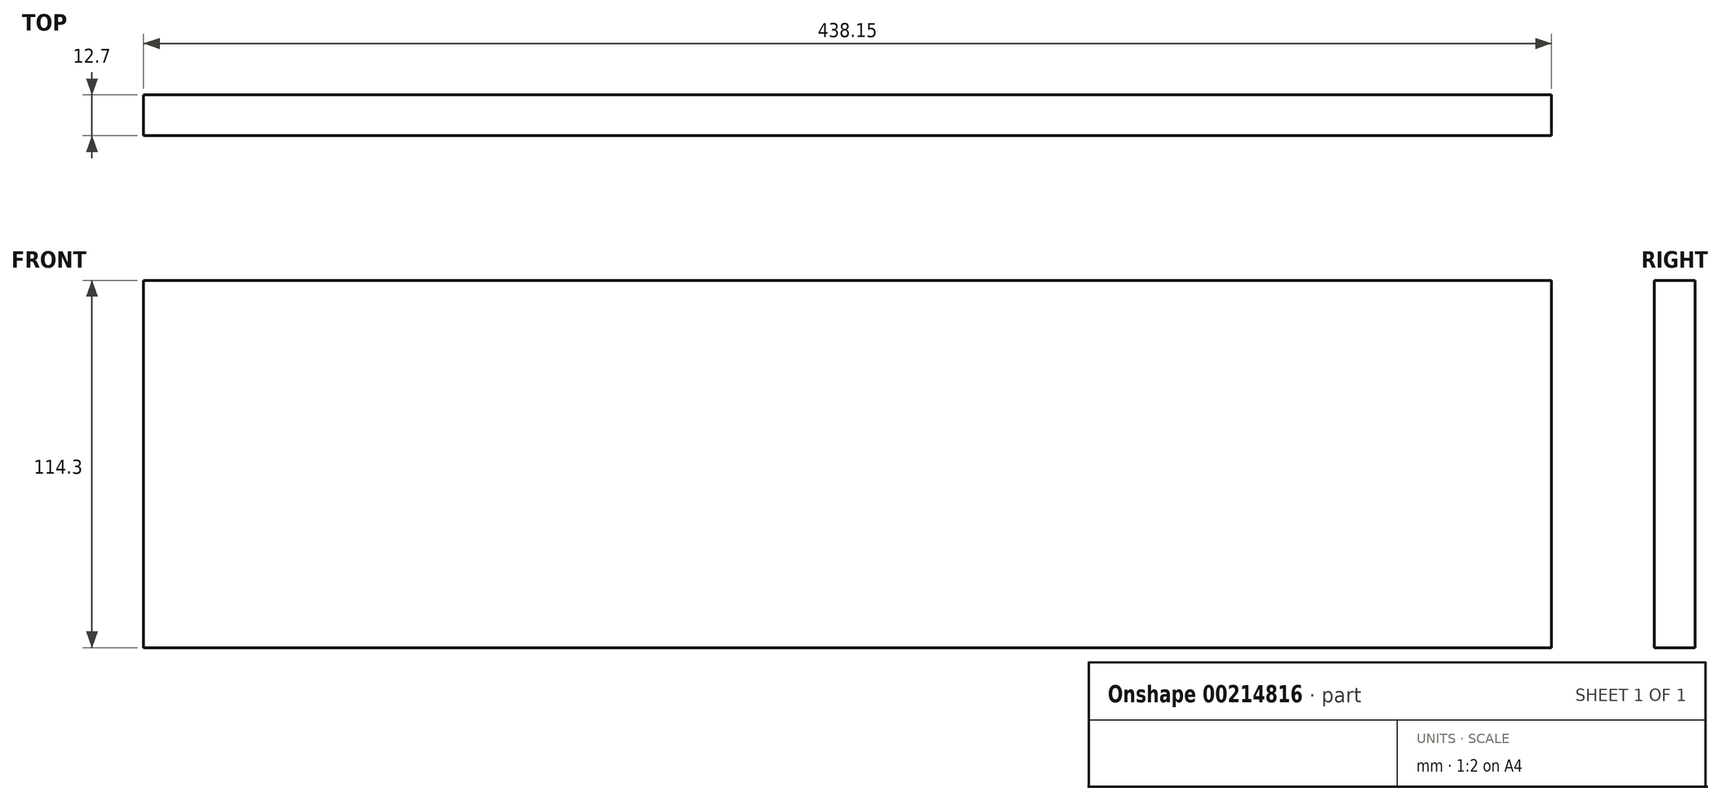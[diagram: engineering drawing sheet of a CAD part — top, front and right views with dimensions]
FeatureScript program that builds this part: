
annotation { "Feature Type Name" : "Feature", "Feature Type Description" : "" }
export const myFeature = defineFeature(function(context is Context, id is Id, definition is map)
    precondition{}
    {
        {
            var Q0;
            Q0=qCreatedBy(makeId("Front.planeOp"),FACE);
            var sketch = newSketch(context, id + "F0", { "sketchPlane" : qUnion([Q0])});
            skLineSegment(sketch, "E0.bottom", {"start": v(0, 0) * mm, "end": v(438.15, 0) * mm});
            skLineSegment(sketch, "E0.top", {"start": v(0, -114.3) * mm, "end": v(438.15, -114.3) * mm});
            skLineSegment(sketch, "E0.left", {"start": v(0, 0) * mm, "end": v(0, -114.3) * mm});
            skLineSegment(sketch, "E0.right", {"start": v(438.15, 0) * mm, "end": v(438.15, -114.3) * mm});
            skSolve(sketch);
        }
        {
            var Q0;
            Q0=makeQuery(id+"F0.imprint","IMPRINT",FACE,{"disambiguationData":[TD([[makeQuery(id+"F0.imprint","IMPRINT",EDGE,{"derivedFrom":sQuery(id+"F0.wireOp",EDGE,"E0.bottom")}),-1.0]])]});
            extrude(context, id + "F1", {"entities" : qUnion([Q0]), "depth" : 12.7 * mm});
        }
    });
